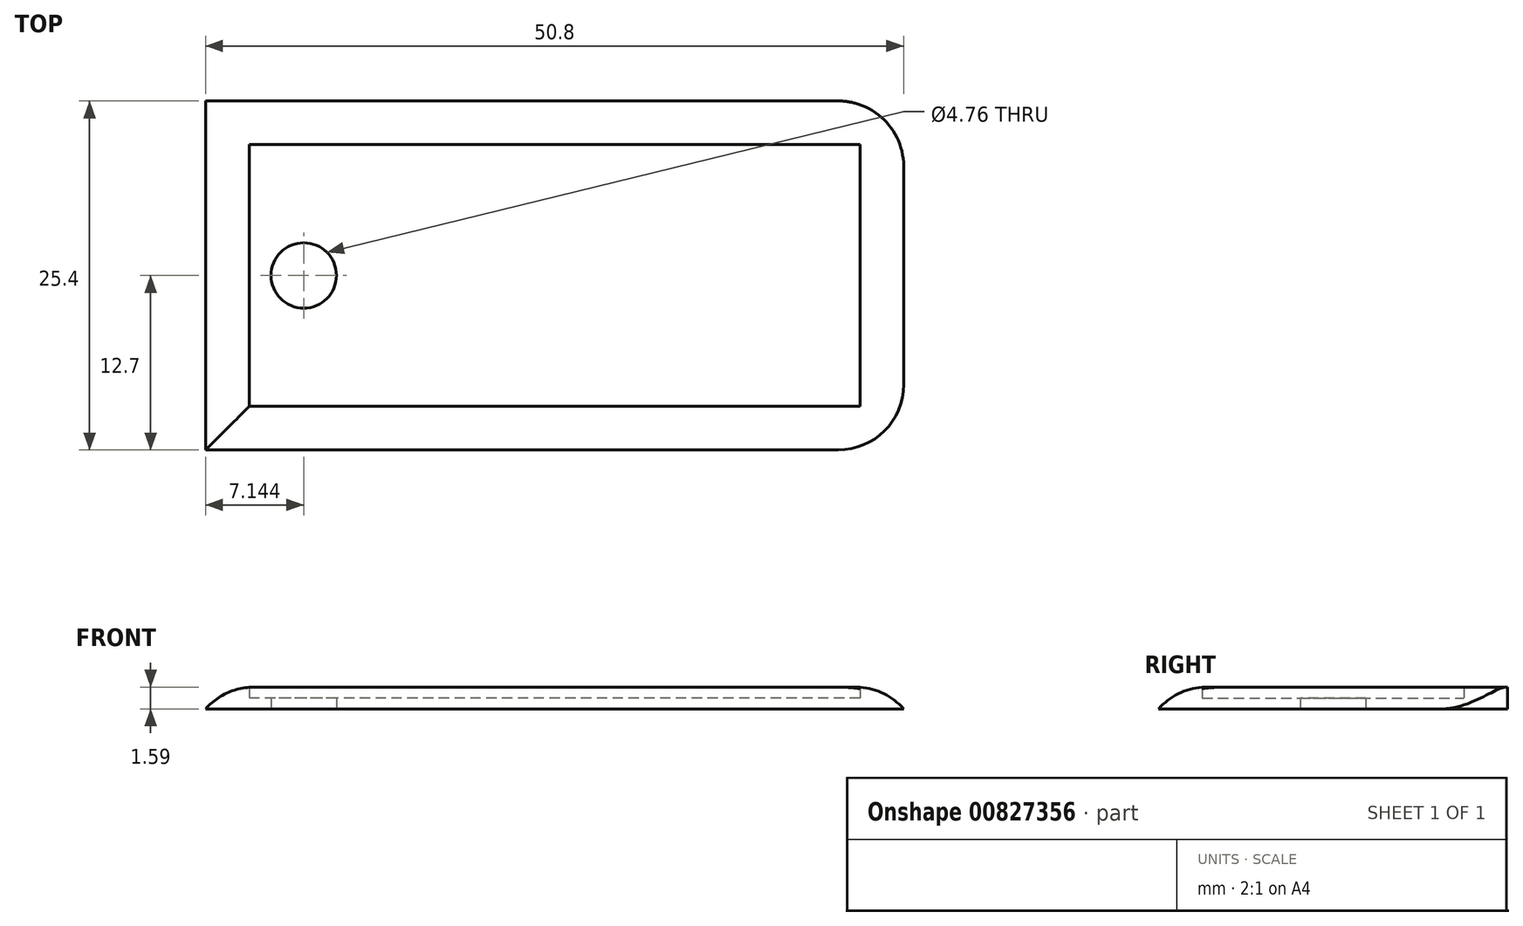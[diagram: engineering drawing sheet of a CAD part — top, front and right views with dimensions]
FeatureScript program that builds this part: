
annotation { "Feature Type Name" : "Feature", "Feature Type Description" : "" }
export const myFeature = defineFeature(function(context is Context, id is Id, definition is map)
    precondition{}
    {
        {
            var Q0;
            Q0=qCreatedBy(makeId("Top.planeOp"),FACE);
            var sketch = newSketch(context, id + "F0", { "sketchPlane" : qUnion([Q0])});
            skLineSegment(sketch, "E0.bottom", {"start": v(0, 25.4) * mm, "end": v(50.8, 25.4) * mm});
            skLineSegment(sketch, "E0.top", {"start": v(0, 0) * mm, "end": v(50.8, 0) * mm});
            skLineSegment(sketch, "E0.left", {"start": v(0, 25.4) * mm, "end": v(0, 0) * mm});
            skLineSegment(sketch, "E0.right", {"start": v(50.8, 25.4) * mm, "end": v(50.8, 0) * mm});
            skCircle(sketch, "E1", {"center": v(7.14, 12.7) * mm, "radius": 2.38 * mm});
            skPoint(sketch, "E2", {"position": v(0, 12.7) * mm});
            skLineSegment(sketch, "E3.bottom", {"start": v(3.18, 22.22) * mm, "end": v(47.63, 22.22) * mm});
            skLineSegment(sketch, "E3.top", {"start": v(3.18, 3.17) * mm, "end": v(47.63, 3.17) * mm});
            skLineSegment(sketch, "E3.left", {"start": v(3.18, 22.22) * mm, "end": v(3.18, 3.17) * mm});
            skLineSegment(sketch, "E3.right", {"start": v(47.63, 22.22) * mm, "end": v(47.63, 3.17) * mm});
            skSolve(sketch);
        }
        {
            var Q0;
            Q0=makeQuery(id+"F0.imprint","IMPRINT",FACE,{"disambiguationData":[TD([[makeQuery(id+"F0.imprint","IMPRINT",EDGE,{"derivedFrom":sQuery(id+"F0.wireOp",EDGE,"E1")}),-1.0]])]});
            var Q1;
            Q1=makeQuery(id+"F0.imprint","IMPRINT",FACE,{"disambiguationData":[TD([[makeQuery(id+"F0.imprint","IMPRINT",EDGE,{"derivedFrom":sQuery(id+"F0.wireOp",EDGE,"E0.bottom")}),-1.0]])]});
            extrude(context, id + "F1", {"entities" : qUnion([Q0, Q1]), "depth" : 0.8 * mm, "offsetDistance" : 25.4 * mm});
        }
        {
            var Q0;
            Q0 = qSketchRegion(id + "F0", true);
            extrude(context, id + "F2", {"entities" : qUnion([Q0]), "operationType" : NewBodyOperationType.ADD, "depth" : 1.59 * mm, "offsetDistance" : 25.4 * mm});
        }
        {
            var Q0;
            Q0=makeQuery(id+"F2.opExtrude","SWEPT_EDGE",EDGE,{"disambiguationData":[OSD([sQuery(id+"F0.wireOp",EDGE,"E0.top"),sQuery(id+"F0.wireOp",EDGE,"E0.right")])]});
            fillet(context, id + "F3", {"entities" : qUnion([Q0]), "radius" : 4.76 * mm, "tangentPropagation" : true, "allowEdgeOverflow" : false});
        }
        {
            var Q0;
            Q0=makeQuery(id+"F2.opExtrude","SWEPT_EDGE",EDGE,{"disambiguationData":[OSD([sQuery(id+"F0.wireOp",EDGE,"E0.bottom"),sQuery(id+"F0.wireOp",EDGE,"E0.right")])]});
            var Q1;
            Q1=makeQuery(id+"F2.opExtrude","CAP_EDGE",EDGE,{"disambiguationData":[OSD([sQuery(id+"F0.wireOp",EDGE,"E0.top")])],"isStart":false});
            var Q2;
            Q2=makeQuery(id+"F2.opExtrude","CAP_EDGE",EDGE,{"disambiguationData":[OSD([sQuery(id+"F0.wireOp",EDGE,"E0.left")])],"isStart":true});
            fillet(context, id + "F4", {"entities" : qUnion([Q0, Q1, Q2]), "radius" : 4.76 * mm, "tangentPropagation" : true, "allowEdgeOverflow" : false});
        }
        {
            var Q0;
            {var subQ0=sQuery(id+"F0.wireOp",EDGE,"E0.left");Q0=makeQuery(id+"F4.opFillet","BLEND_EDGE",EDGE,{"blendedFrom":[makeQuery(id+"F2.opExtrude","CAP_EDGE",EDGE,{"disambiguationData":[OSD([sQuery(id+"F0.wireOp",EDGE,"E0.top")])],"isStart":false}),makeQuery(id+"F2.boolean.opBoolean","MERGE",FACE,{"derivedFrom":[makeQuery(id+"F1.opExtrude","SWEPT_FACE",FACE,{"disambiguationData":[OSD([subQ0])]}),makeQuery(id+"F2.opExtrude","SWEPT_FACE",FACE,{"disambiguationData":[OSD([subQ0])]})]})],"blendedInto":[makeQuery(id+"F2.boolean.opBoolean","MERGE",FACE,{"derivedFrom":[makeQuery(id+"F1.opExtrude","SWEPT_FACE",FACE,{"disambiguationData":[OSD([subQ0])]}),makeQuery(id+"F2.opExtrude","SWEPT_FACE",FACE,{"disambiguationData":[OSD([subQ0])]})]})]});}
            fillet(context, id + "F5", {"entities" : qUnion([Q0]), "radius" : 4.76 * mm, "tangentPropagation" : true, "allowEdgeOverflow" : false});
        }
    });
